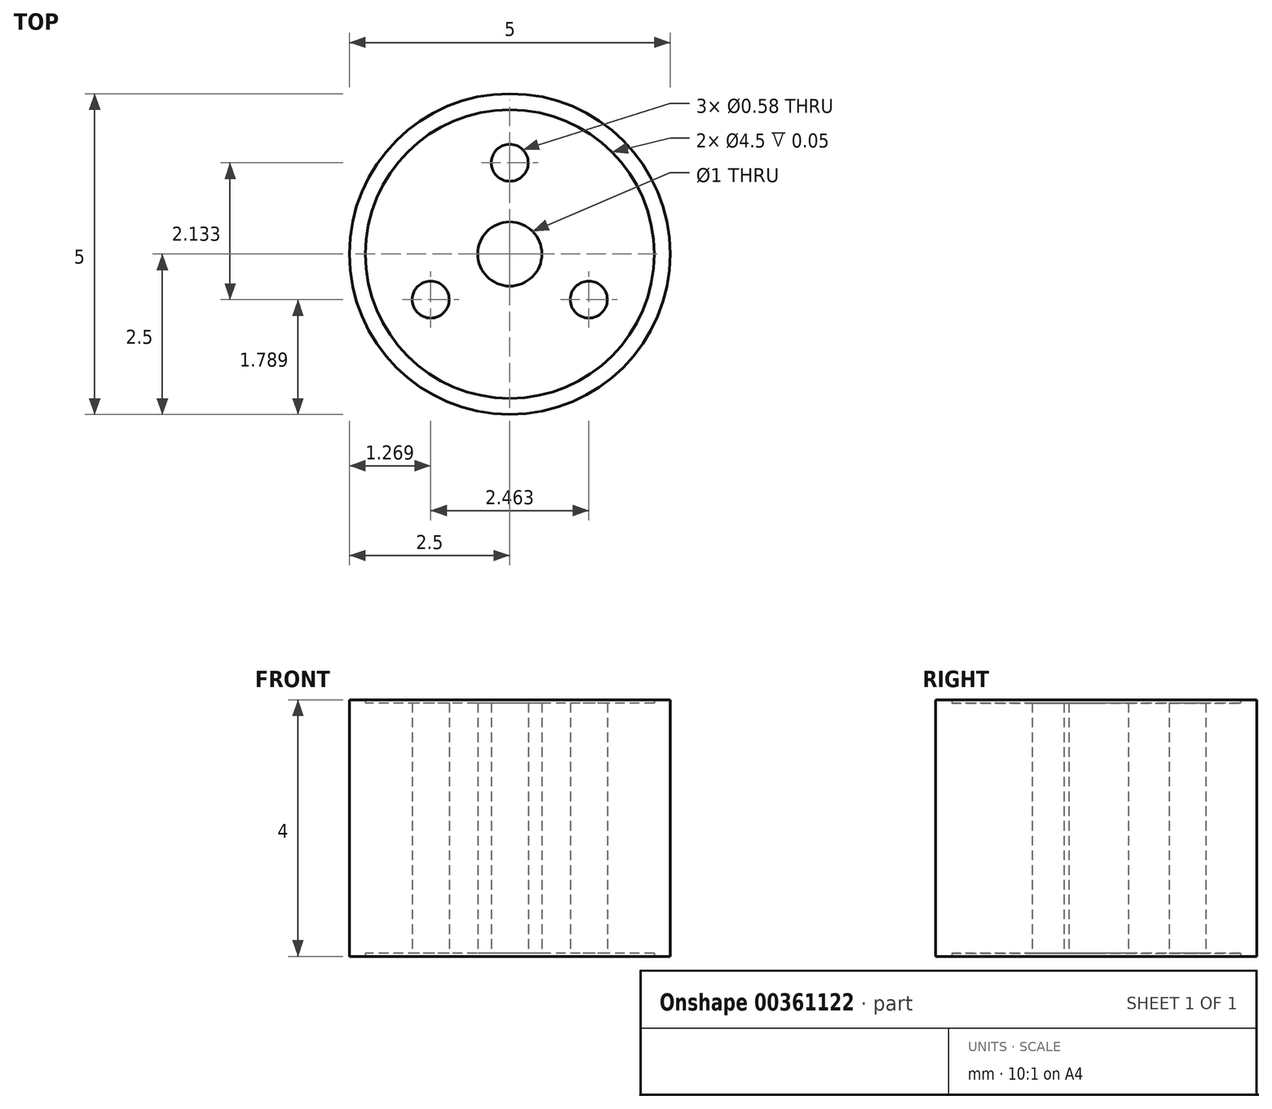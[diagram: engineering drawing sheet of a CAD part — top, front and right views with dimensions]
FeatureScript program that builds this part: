
annotation { "Feature Type Name" : "Feature", "Feature Type Description" : "" }
export const myFeature = defineFeature(function(context is Context, id is Id, definition is map)
    precondition{}
    {
        {
            var Q0;
            Q0=qCreatedBy(makeId("Top.planeOp"),FACE);
            var sketch = newSketch(context, id + "F0", { "sketchPlane" : qUnion([Q0])});
            skCircle(sketch, "E0", {"center": v(0, 0) * mm, "radius": 2.5 * mm});
            skCircle(sketch, "E1", {"center": v(0, 0) * mm, "radius": 2.25 * mm});
            skCircle(sketch, "E2", {"center": v(0, 0) * mm, "radius": 0.5 * mm});
            skCircle(sketch, "E3", {"center": v(0, 1.42) * mm, "radius": 0.29 * mm});
            skCircle(sketch, "E4.1.0", {"center": v(-1.23, -0.71) * mm, "radius": 0.29 * mm});
            skCircle(sketch, "E4.2.0", {"center": v(1.23, -0.71) * mm, "radius": 0.29 * mm});
            skSolve(sketch);
        }
        {
            var Q0;
            Q0=makeQuery(id+"F0.imprint","IMPRINT",FACE,{"disambiguationData":[TD([[makeQuery(id+"F0.imprint","IMPRINT",EDGE,{"derivedFrom":sQuery(id+"F0.wireOp",EDGE,"E1")}),1.0]])]});
            extrude(context, id + "F1", {"entities" : qUnion([Q0]), "endBound" : BoundingType.SYMMETRIC, "depth" : 3.9 * mm});
        }
        {
            var Q0;
            Q0=makeQuery(id+"F0.imprint","IMPRINT",FACE,{"disambiguationData":[TD([[makeQuery(id+"F0.imprint","IMPRINT",EDGE,{"derivedFrom":sQuery(id+"F0.wireOp",EDGE,"E0")}),1.0]])]});
            extrude(context, id + "F2", {"entities" : qUnion([Q0]), "operationType" : NewBodyOperationType.ADD, "endBound" : BoundingType.SYMMETRIC, "depth" : 4 * mm});
        }
    });
